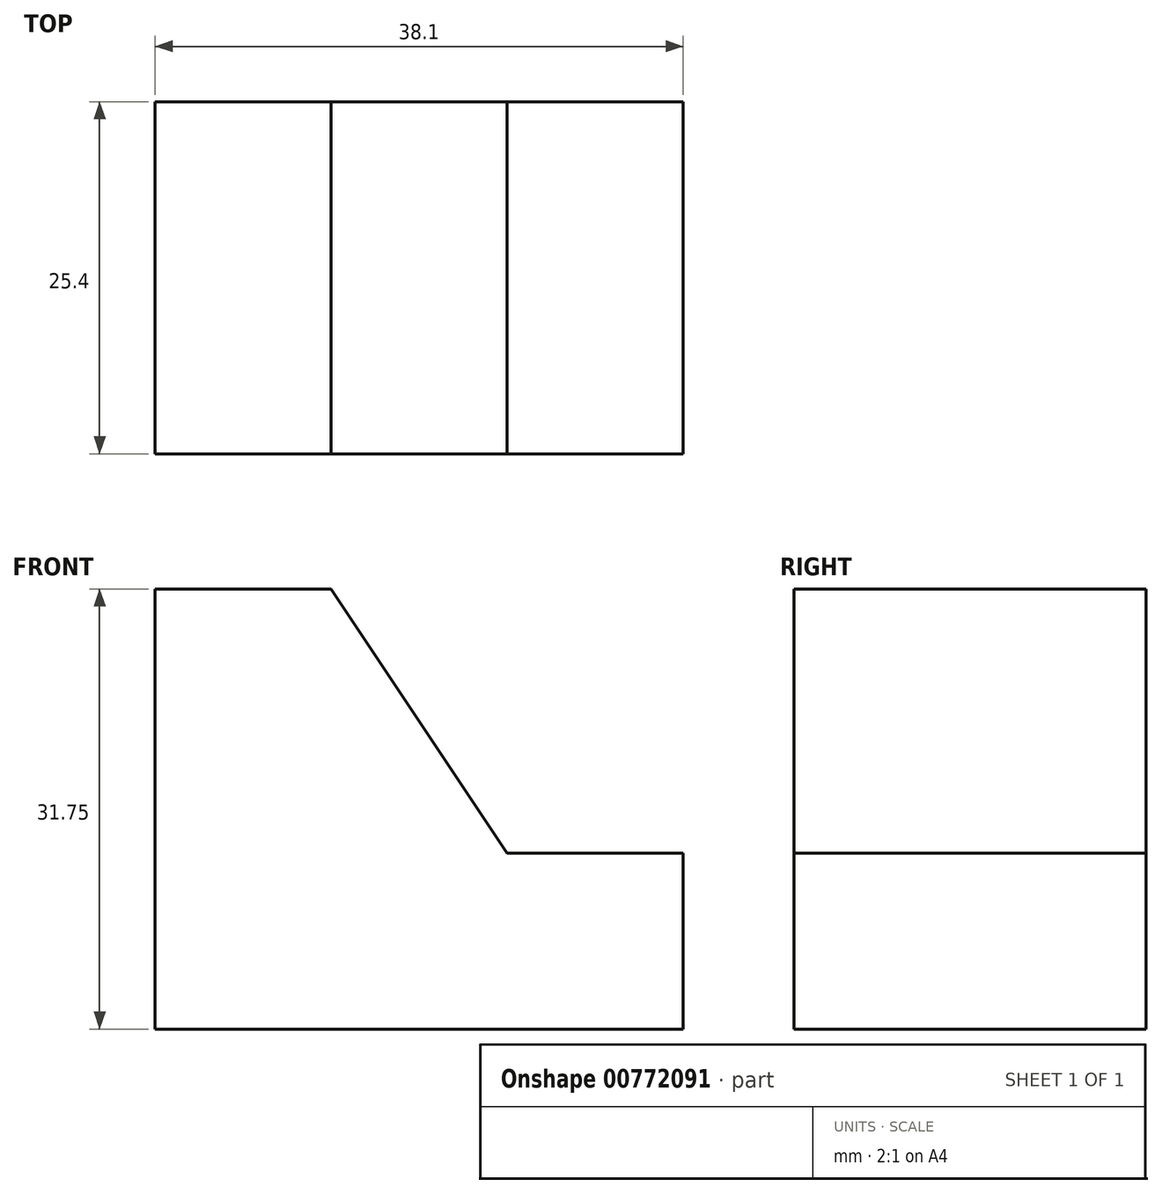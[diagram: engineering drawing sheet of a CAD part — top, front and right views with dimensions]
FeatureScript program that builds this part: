
annotation { "Feature Type Name" : "Feature", "Feature Type Description" : "" }
export const myFeature = defineFeature(function(context is Context, id is Id, definition is map)
    precondition{}
    {
        {
            var Q0;
            Q0=qCreatedBy(makeId("Front.planeOp"),FACE);
            var sketch = newSketch(context, id + "F0", { "sketchPlane" : qUnion([Q0])});
            skLineSegment(sketch, "E0", {"start": v(0, 0) * mm, "end": v(0, 31.75) * mm});
            skLineSegment(sketch, "E1", {"start": v(0, 0) * mm, "end": v(38.1, 0) * mm});
            skLineSegment(sketch, "E2", {"start": v(0, 31.75) * mm, "end": v(12.7, 31.75) * mm});
            skLineSegment(sketch, "E3", {"start": v(38.1, 0) * mm, "end": v(38.1, 12.7) * mm});
            skLineSegment(sketch, "E4", {"start": v(38.1, 12.7) * mm, "end": v(25.4, 12.7) * mm});
            skLineSegment(sketch, "E5", {"start": v(12.7, 31.75) * mm, "end": v(25.4, 12.7) * mm});
            skSolve(sketch);
        }
        {
            var Q0;
            Q0=makeQuery(id+"F0.imprint","IMPRINT",FACE,{"disambiguationData":[TD([[makeQuery(id+"F0.imprint","IMPRINT",EDGE,{"derivedFrom":sQuery(id+"F0.wireOp",EDGE,"E0")}),-1.0]])]});
            extrude(context, id + "F1", {"entities" : qUnion([Q0]), "depth" : 25.4 * mm, "offsetDistance" : 25.4 * mm});
        }
    });
